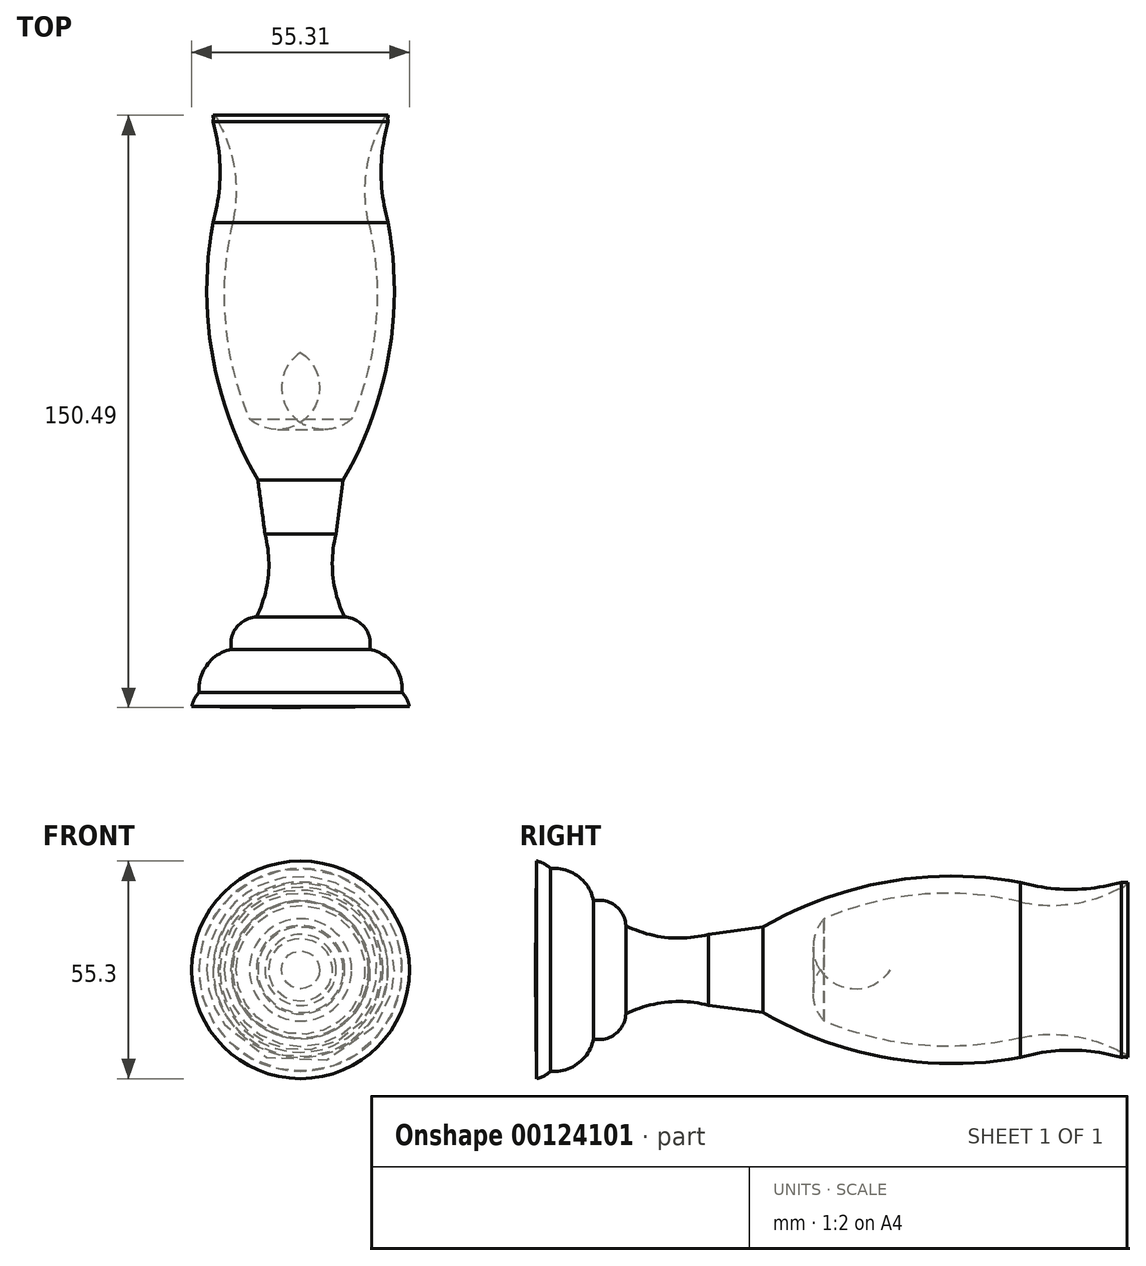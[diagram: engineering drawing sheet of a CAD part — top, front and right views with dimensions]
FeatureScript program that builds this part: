
annotation { "Feature Type Name" : "Feature", "Feature Type Description" : "" }
export const myFeature = defineFeature(function(context is Context, id is Id, definition is map)
    precondition{}
    {
        {
            var Q0;
            Q0=qCreatedBy(makeId("Top.planeOp"),FACE);
            var sketch = newSketch(context, id + "F0", { "sketchPlane" : qUnion([Q0])});
            skArc(sketch, "E0", {"start": v(-14.22, 17.73) * mm, "mid": v(-7.1, 15.02) * mm, "end": v(0, 17.73) * mm});
            skArc(sketch, "E1", {"start": v(-3.95, -11.55) * mm, "mid": v(-4.77, -22.27) * mm, "end": v(-1.76, -32.6) * mm});
            skLineSegment(sketch, "E2", {"start": v(-12.98, 94.9) * mm, "end": v(-12.98, -55.6) * mm});
            skArc(sketch, "E3", {"start": v(4.55, -40.83) * mm, "mid": v(3.3, -35.25) * mm, "end": v(-1.76, -32.6) * mm});
            skArc(sketch, "E4", {"start": v(12.75, -51.77) * mm, "mid": v(10.77, -44.71) * mm, "end": v(4.55, -40.83) * mm});
            skArc(sketch, "E5", {"start": v(14.67, -55.32) * mm, "mid": v(13.98, -53.4) * mm, "end": v(12.75, -51.77) * mm});
            skLineSegment(sketch, "E6", {"start": v(-2.13, 2.27) * mm, "end": v(-3.95, -11.55) * mm});
            skLineSegment(sketch, "E7", {"start": v(14.67, -55.32) * mm, "end": v(-12.98, -55.6) * mm});
            skArc(sketch, "E8", {"start": v(-2.13, 2.27) * mm, "mid": v(9.4, 33.92) * mm, "end": v(9.28, 67.61) * mm});
            skArc(sketch, "E9", {"start": v(9.28, 93.23) * mm, "mid": v(7.45, 80.42) * mm, "end": v(9.28, 67.61) * mm});
            skArc(sketch, "E10", {"start": v(0, 17.73) * mm, "mid": v(6.17, 42.33) * mm, "end": v(4.26, 67.61) * mm});
            skArc(sketch, "E11", {"start": v(7.94, 93.23) * mm, "mid": v(3.78, 80.76) * mm, "end": v(4.26, 67.61) * mm});
            skArc(sketch, "E12", {"start": v(9.28, 94.9) * mm, "mid": v(8.37, 94.26) * mm, "end": v(7.94, 93.23) * mm});
            skArc(sketch, "E13", {"start": v(9.28, 94.9) * mm, "mid": v(9.17, 94.06) * mm, "end": v(9.28, 93.23) * mm});
            skSolve(sketch);
        }
        {
            var Q0;
            {var subQ0=sQuery(id+"F0.wireOp",EDGE,"E0");Q0=makeQuery(id+"F0.imprint","IMPRINT",FACE,{"disambiguationData":[TD([[makeQuery(id+"F0.imprint","IMPRINT",EDGE,{"derivedFrom":subQ0}),-1.0]])]});}
            var Q1;
            Q1=sQuery(id+"F0.wireOp",EDGE,"E2");
            revolve(context, id + "F1", {"entities" : qUnion([Q0]), "axis" : qUnion([Q1]), "revolveType" : RevolveType.FULL});
        }
    });
